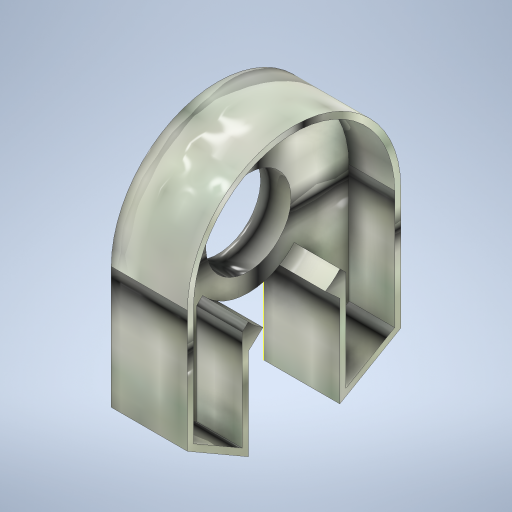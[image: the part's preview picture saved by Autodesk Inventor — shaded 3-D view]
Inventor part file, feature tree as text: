
AUTODESK INVENTOR PART (.ipt)
format: ipt  version: 2023 (Build 270158000, 158)  size: 820,224 bytes
history: native  units: mm
features: extrude x2, sketch x1
ambient origin geometry x8: Origin, YZ Plane, XZ Plane, XY Plane, X Axis, Y Axis, Z Axis, Center Point
bodies: Body1 (feature_tree)
feature tree (3):
  extrude  "Extrusion3"  Depth=15.0mm
  extrude  "Extrusion4"  Depth=2.0mm
  sketch  "Sketch2"  dims[d0=70.0mm d9=15.0mm d17=6.0mm d27=25.0mm d28=0.0mm d29=10.0mm d30=0.0mm d32=40.0mm d43=20.0mm d44=30.0deg d45=30.0mm d47=2.0mm d48=45.0deg d49=23.09157mm d50=1.306712mm d51=30.659518mm d52=29.0mm d54=2.990754mm d23=0.5mm d24=0.872665mm d25=0.5mm d26=0.872665mm]
